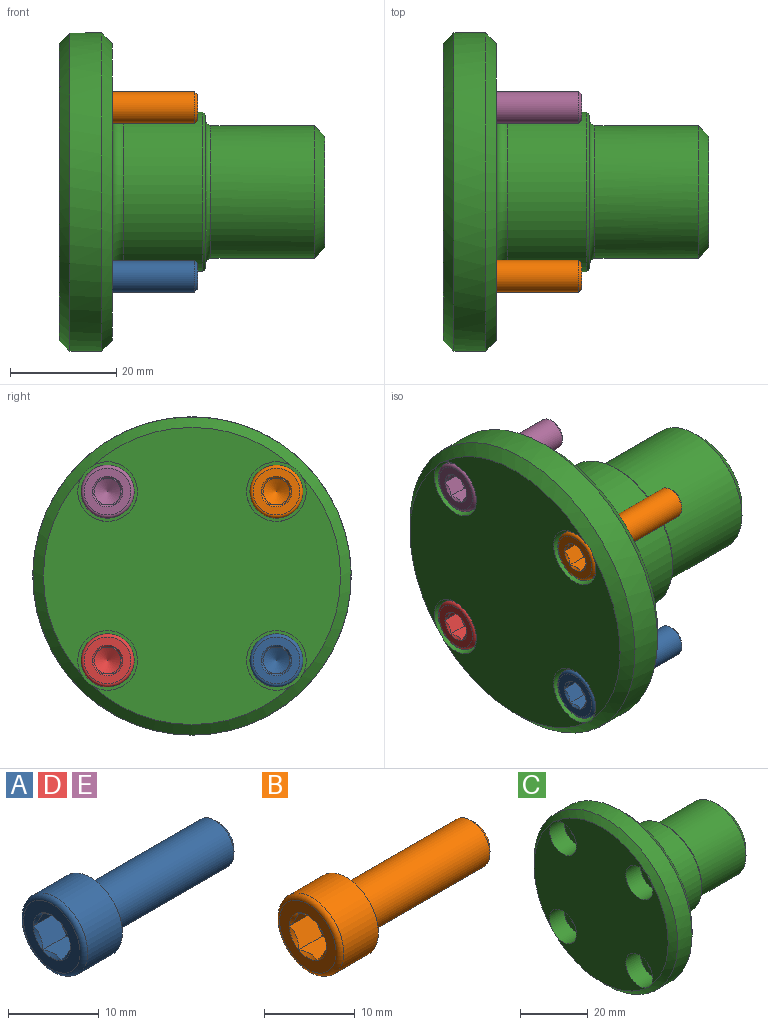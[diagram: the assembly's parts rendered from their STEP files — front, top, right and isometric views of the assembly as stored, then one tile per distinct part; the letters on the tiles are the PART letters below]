
ASSEMBLY  parts=5 mates=4
PART A: 24 faces, bbox 26x10.8x10.8 mm
  f0: cone r=1.25mm half-angle=60deg, axis (-1,0,0), area 22.7mm2, adj f13,f14,f15,f16,f17,f18
  f1: cone r=2.69mm half-angle=45deg, axis (-1,0,0), area 6.4mm2, adj f9,f10,f11,f12,f19,f20,f23
  f2: torus R=4.4mm, axis (-1,0,0), area 28.3mm2, adj f3,f23
  f3: cylinder r=5mm len=10mm, axis (-1,0,0), area 169.6mm2, adj f2,f22
  f4: torus R=3.4mm, axis (-1,0,0), area 6.3mm2, adj f5,f22
  f5: cone r=3.09mm half-angle=19.2deg, axis (-1,0,0), area 8.8mm2, adj f4,f6
  f6: torus R=3.25mm, axis (-1,0,0), area 1.6mm2, adj f5,f7
  f7: cylinder r=3mm len=18.71mm, axis (-1,0,0), area 352.6mm2, adj f6,f8
  f8: cone r=2.69mm half-angle=45deg, axis (-1,0,0), area 14.7mm2, adj f7,f21
  f9: plane 3.7x2.5mm, normal (0,-0.87,0.5), area 9.9mm2, adj f1,f10,f11,f15,f16
  f10: plane 3.7x2.89mm, normal (0,0,1), area 9.9mm2, adj f1,f9,f12,f16,f17
  f11: plane 3.7x2.5mm, normal (0,-0.87,-0.5), area 9.9mm2, adj f1,f9,f14,f15,f19
  f12: plane 3.7x2.5mm, normal (0,0.87,0.5), area 9.9mm2, adj f1,f10,f17,f18,f20
  f13: plane 2.17x1.25mm, normal (-1,0,0), area 0.3mm2, adj f0,f19,f20
  f14: plane 2.17x1.25mm, normal (-1,0,0), area 0.3mm2, adj f0,f11,f19
  f15: plane 2.5x0.72mm, normal (-1,0,0), area 0.3mm2, adj f0,f9,f11
  f16: plane 2.17x1.25mm, normal (-1,0,0), area 0.3mm2, adj f0,f9,f10
  f17: plane 2.17x1.25mm, normal (-1,0,0), area 0.3mm2, adj f0,f10,f12
  f18: plane 2.5x0.72mm, normal (-1,0,0), area 0.3mm2, adj f0,f12,f20
  f19: plane 3.7x2.89mm, normal (0,0,-1), area 9.9mm2, adj f1,f11,f13,f14,f20
  f20: plane 3.7x2.5mm, normal (0,0.87,-0.5), area 9.9mm2, adj f1,f12,f13,f18,f19
  f21: plane 4.77x4.77mm, normal (1,0,0), area 17.9mm2, adj f8
  f22: plane 10x10mm, normal (1,0,0), area 42.2mm2, adj f3,f4
  f23: plane 8.8x8.8mm, normal (-1,0,0), area 34.6mm2, adj f1,f2
PART B: 24 faces, bbox 26x10.8x10.8 mm
  f0: cone r=1.25mm half-angle=60deg, axis (-1,0,0), area 22.7mm2, adj f13,f14,f15,f16,f17,f18
  f1: cone r=2.69mm half-angle=45deg, axis (-1,0,0), area 6.4mm2, adj f9,f10,f11,f12,f19,f20,f23
  f2: torus R=4.4mm, axis (-1,0,0), area 28.3mm2, adj f3,f23
  f3: cylinder r=5mm len=10mm, axis (-1,0,0), area 169.6mm2, adj f2,f22
  f4: torus R=3.4mm, axis (-1,0,0), area 6.3mm2, adj f5,f22
  f5: cone r=3.09mm half-angle=19.2deg, axis (-1,0,0), area 8.8mm2, adj f4,f6
  f6: torus R=3.25mm, axis (-1,0,0), area 1.6mm2, adj f5,f7
  f7: cylinder r=3mm len=18.71mm, axis (-1,0,0), area 352.6mm2, adj f6,f8
  f8: cone r=2.69mm half-angle=45deg, axis (-1,0,0), area 14.7mm2, adj f7,f21
  f9: plane 3.7x2.5mm, normal (0,-0.87,0.5), area 9.9mm2, adj f1,f10,f11,f15,f16
  f10: plane 3.7x2.89mm, normal (0,0,1), area 9.9mm2, adj f1,f9,f12,f16,f17
  f11: plane 3.7x2.5mm, normal (0,-0.87,-0.5), area 9.9mm2, adj f1,f9,f14,f15,f19
  f12: plane 3.7x2.5mm, normal (0,0.87,0.5), area 9.9mm2, adj f1,f10,f17,f18,f20
  f13: plane 2.17x1.25mm, normal (-1,0,0), area 0.3mm2, adj f0,f19,f20
  f14: plane 2.17x1.25mm, normal (-1,0,0), area 0.3mm2, adj f0,f11,f19
  f15: plane 2.5x0.72mm, normal (-1,0,0), area 0.3mm2, adj f0,f9,f11
  f16: plane 2.17x1.25mm, normal (-1,0,0), area 0.3mm2, adj f0,f9,f10
  f17: plane 2.17x1.25mm, normal (-1,0,0), area 0.3mm2, adj f0,f10,f12
  f18: plane 2.5x0.72mm, normal (-1,0,0), area 0.3mm2, adj f0,f12,f20
  f19: plane 3.7x2.89mm, normal (0,0,-1), area 9.9mm2, adj f1,f11,f13,f14,f20
  f20: plane 3.7x2.5mm, normal (0,0.87,-0.5), area 9.9mm2, adj f1,f12,f13,f18,f19
  f21: plane 4.77x4.77mm, normal (1,0,0), area 17.9mm2, adj f8
  f22: plane 10x10mm, normal (1,0,0), area 42.2mm2, adj f3,f4
  f23: plane 8.8x8.8mm, normal (-1,0,0), area 34.6mm2, adj f1,f2
PART C: 25 faces, bbox 50x60x60 mm
  f0: cone r=30mm half-angle=45deg, axis (1,0,0), area 514.1mm2, adj f1,f7,f15,f18,f21,f24
  f1: plane 56x56mm, normal (-1,0,0), area 2066.3mm2, adj f0,f15,f18,f21,f24
  f2: plane 21x21mm, normal (1,0,0), area 346.4mm2, adj f8
  f3: cylinder r=12.5mm len=25mm, axis (1,0,0), area 1525.2mm2, adj f8,f11
  f4: cone r=15mm half-angle=87deg, axis (-1,0,0), area 92.6mm2, adj f11,f12
  f5: cylinder r=15mm len=30mm, axis (1,0,0), area 1413.7mm2, adj f10,f12
  f6: plane 56x56mm, normal (1,0,0), area 1418.2mm2, adj f9,f10,f13,f16,f19,f22
  f7: cylinder r=30mm len=60mm, axis (1,0,0), area 1131mm2, adj f0,f9
  f8: cone r=10.5mm half-angle=45deg, axis (-1,0,0), area 204.4mm2, adj f2,f3
  f9: cone r=28mm half-angle=45deg, axis (-1,0,0), area 515.4mm2, adj f6,f7
  f10: torus R=17mm, axis (-1,0,0), area 310.4mm2, adj f5,f6
  f11: torus R=13.5mm, axis (1,0,0), area 122.5mm2, adj f3,f4
  f12: cone r=14.5mm half-angle=43.5deg, axis (-1,0,0), area 67.2mm2, adj f4,f5
  f13: cylinder r=3.3mm len=6.6mm, axis (-1,0,0), area 80.3mm2, adj f6,f14
  f14: plane 11.25x11.25mm, normal (-1,0,0), area 65.2mm2, adj f13,f15
  f15: cylinder r=5.62mm len=11.25mm, axis (-1,0,0), area 216.3mm2, adj f0,f1,f14
  f16: cylinder r=3.3mm len=6.6mm, axis (-1,0,0), area 80.3mm2, adj f6,f17
  f17: plane 11.25x11.25mm, normal (-1,0,0), area 65.2mm2, adj f16,f18
  f18: cylinder r=5.62mm len=11.25mm, axis (-1,0,0), area 216.3mm2, adj f0,f1,f17
  f19: cylinder r=3.3mm len=6.6mm, axis (-1,0,0), area 80.3mm2, adj f6,f20
  f20: plane 11.25x11.25mm, normal (-1,0,0), area 65.2mm2, adj f19,f21
  f21: cylinder r=5.62mm len=11.25mm, axis (-1,0,0), area 216.3mm2, adj f0,f1,f20
  f22: cylinder r=3.3mm len=6.6mm, axis (-1,0,0), area 80.3mm2, adj f6,f23
  f23: plane 11.25x11.25mm, normal (-1,0,0), area 65.2mm2, adj f22,f24
  f24: cylinder r=5.62mm len=11.25mm, axis (-1,0,0), area 216.3mm2, adj f0,f1,f23
PART D: same geometry as A
PART E: same geometry as A
PLACE A t=(-58.62,-15.91,-15.91)mm
PLACE B at identity
PLACE C at identity
PLACE D t=(-58.63,15.91,-15.91)mm
PLACE E t=(-58.63,15.91,15.91)mm
MATE fastened D.f0 <-> C.f19  axis (1,0,0) through (-58.63,15.91,-15.91)mm
MATE fastened E.f0 <-> C.f22  axis (1,0,0) through (-58.63,15.91,15.91)mm
MATE fastened A.f0 <-> C.f16  axis (1,0,0) through (-58.62,-15.91,-15.91)mm
MATE fastened B.f0 <-> C.f13  axis (1,0,0) through (-58.62,-15.91,15.91)mm
